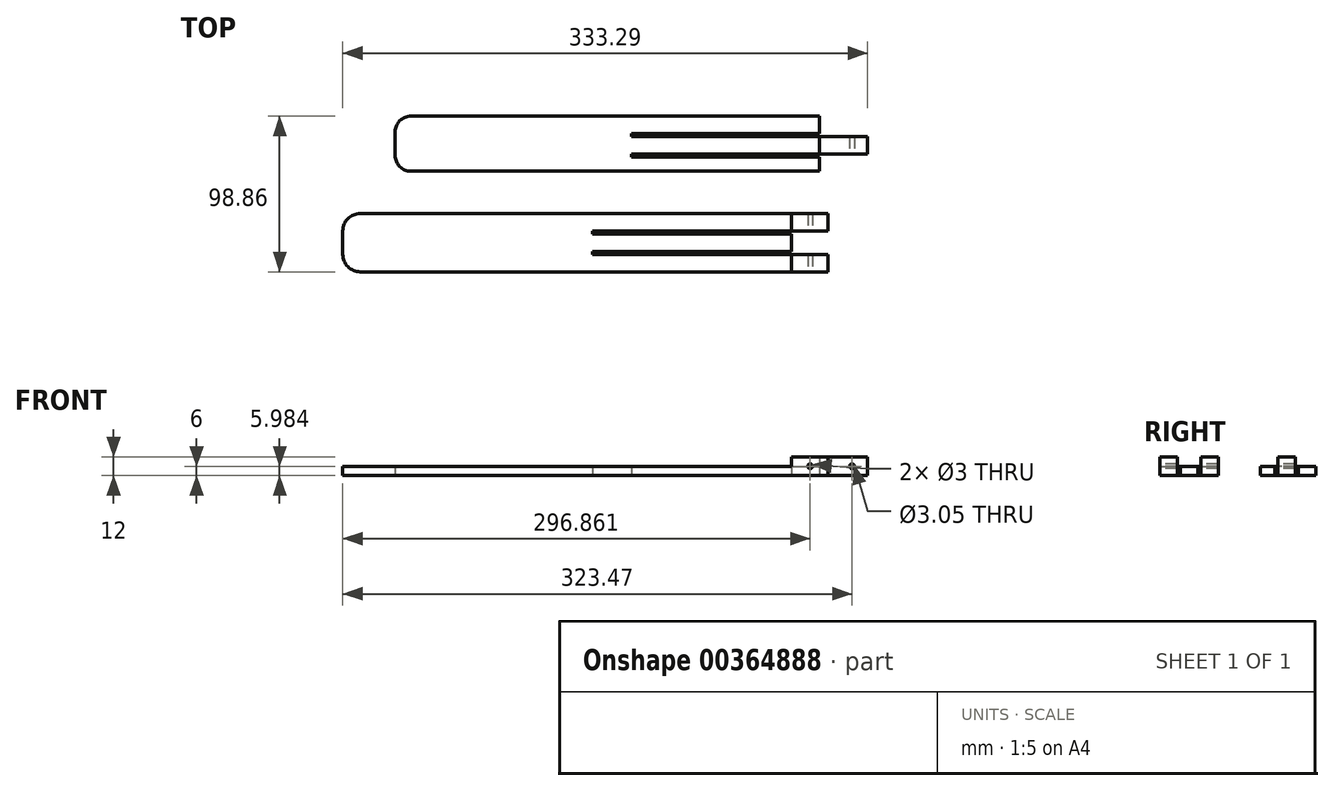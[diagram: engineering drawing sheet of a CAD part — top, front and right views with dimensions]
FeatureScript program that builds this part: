
annotation { "Feature Type Name" : "Feature", "Feature Type Description" : "" }
export const myFeature = defineFeature(function(context is Context, id is Id, definition is map)
    precondition{}
    {
        {
            var Q0;
            Q0=qCreatedBy(makeId("Top.planeOp"),FACE);
            var sketch = newSketch(context, id + "F0", { "sketchPlane" : qUnion([Q0])});
            skLineSegment(sketch, "E0.bottom", {"start": v(-150, 17.5) * mm, "end": v(119.34, 17.5) * mm});
            skLineSegment(sketch, "E0.top", {"start": v(-150, -17.5) * mm, "end": v(119.34, -17.5) * mm});
            skLineSegment(sketch, "E0.left", {"start": v(-150, 17.5) * mm, "end": v(-150, -17.5) * mm});
            skPoint(sketch, "E0.middle", {"position": v(0, 0) * mm});
            skLineSegment(sketch, "E1", {"start": v(0, 6.5) * mm, "end": v(119.34, 6.5) * mm});
            skLineSegment(sketch, "E2", {"start": v(0, 4.5) * mm, "end": v(150, 4.5) * mm});
            skLineSegment(sketch, "E3", {"start": v(0, -8.5) * mm, "end": v(119.34, -8.5) * mm});
            skLineSegment(sketch, "E4", {"start": v(0, -6.5) * mm, "end": v(150, -6.5) * mm});
            skLineSegment(sketch, "E5", {"start": v(0, -6.5) * mm, "end": v(0, -8.5) * mm});
            skLineSegment(sketch, "E6", {"start": v(0, 6.5) * mm, "end": v(0, 4.5) * mm});
            skLineSegment(sketch, "E7.trimOffspring", {"start": v(150, 4.5) * mm, "end": v(150, -6.5) * mm});
            skLineSegment(sketch, "E8", {"start": v(119.34, 17.5) * mm, "end": v(119.34, 6.5) * mm});
            skPoint(sketch, "E0.right.start.orphan", {"position": v(150, 17.5) * mm});
            skPoint(sketch, "E9.trimOffspring.start.orphan", {"position": v(150, -8.5) * mm});
            skPoint(sketch, "E10.orphan", {"position": v(150, -17.5) * mm});
            skLineSegment(sketch, "E11.trimOffspring", {"start": v(119.34, -8.5) * mm, "end": v(119.34, -17.5) * mm});
            skSolve(sketch);
        }
        {
            var Q0;
            Q0=makeQuery(id+"F0.imprint","IMPRINT",FACE,{"disambiguationData":[TD([[makeQuery(id+"F0.imprint","IMPRINT",EDGE,{"derivedFrom":sQuery(id+"F0.wireOp",EDGE,"E0.bottom")}),-1.0]])]});
            extrude(context, id + "F1", {"entities" : qUnion([Q0]), "depth" : 6 * mm});
        }
        {
            var Q0;
            Q0=makeQuery(id+"F1.opExtrude","SWEPT_EDGE",EDGE,{"disambiguationData":[OSD([sQuery(id+"F0.wireOp",EDGE,"E0.top"),sQuery(id+"F0.wireOp",EDGE,"E0.left")])]});
            var Q1;
            Q1=makeQuery(id+"F1.opExtrude","SWEPT_EDGE",EDGE,{"disambiguationData":[OSD([sQuery(id+"F0.wireOp",EDGE,"E0.bottom"),sQuery(id+"F0.wireOp",EDGE,"E0.left")])]});
            fillet(context, id + "F2", {"entities" : qUnion([Q0, Q1]), "radius" : 10 * mm, "tangentPropagation" : true, "allowEdgeOverflow" : false});
        }
        {
            var Q0;
            Q0=makeQuery(id+"F1.opExtrude","CAP_FACE",FACE,{"disambiguationData":[OSD([sQuery(id+"F0.wireOp",EDGE,"E0.bottom"),sQuery(id+"F0.wireOp",EDGE,"E0.top"),sQuery(id+"F0.wireOp",EDGE,"E0.left"),sQuery(id+"F0.wireOp",EDGE,"E1"),sQuery(id+"F0.wireOp",EDGE,"E2"),sQuery(id+"F0.wireOp",EDGE,"E3"),sQuery(id+"F0.wireOp",EDGE,"E4"),sQuery(id+"F0.wireOp",EDGE,"E5"),sQuery(id+"F0.wireOp",EDGE,"E6"),sQuery(id+"F0.wireOp",EDGE,"E7.trimOffspring"),sQuery(id+"F0.wireOp",EDGE,"E8"),sQuery(id+"F0.wireOp",EDGE,"E11.trimOffspring")])],"isStart":false});
            var sketch = newSketch(context, id + "F3", { "sketchPlane" : qUnion([Q0])});
            skLineSegment(sketch, "E12.bottom", {"start": v(119.34, 4.5) * mm, "end": v(150, 4.5) * mm});
            skLineSegment(sketch, "E12.top", {"start": v(119.34, -6.5) * mm, "end": v(150, -6.5) * mm});
            skLineSegment(sketch, "E12.left", {"start": v(119.34, 4.5) * mm, "end": v(119.34, -6.5) * mm});
            skLineSegment(sketch, "E12.right", {"start": v(150, 4.5) * mm, "end": v(150, -6.5) * mm});
            skSolve(sketch);
        }
        {
            var Q0;
            Q0=makeQuery(id+"F3.imprint","IMPRINT",FACE,{"disambiguationData":[TD([[makeQuery(id+"F3.imprint","IMPRINT",EDGE,{"derivedFrom":sQuery(id+"F3.wireOp",EDGE,"E12.bottom")}),-1.0]])]});
            extrude(context, id + "F4", {"entities" : qUnion([Q0]), "operationType" : NewBodyOperationType.ADD, "depth" : 6 * mm});
        }
        {
            var Q0;
            Q0=makeQuery(id+"F4.boolean.opBoolean","MERGE",FACE,{"derivedFrom":[makeQuery(id+"F1.opExtrude","SWEPT_FACE",FACE,{"disambiguationData":[OSD([sQuery(id+"F0.wireOp",EDGE,"E4")])]}),makeQuery(id+"F4.opExtrude","SWEPT_FACE",FACE,{"disambiguationData":[OSD([sQuery(id+"F3.wireOp",EDGE,"E12.top")])]})]});
            var sketch = newSketch(context, id + "F5", { "sketchPlane" : qUnion([Q0])});
            skCircle(sketch, "E13", {"center": v(140.18, 5.98) * mm, "radius": 1.53 * mm});
            skSolve(sketch);
        }
        {
            var Q0;
            Q0=makeQuery(id+"F5.imprint","IMPRINT",FACE,{"disambiguationData":[TD([[makeQuery(id+"F5.imprint","IMPRINT",EDGE,{"derivedFrom":sQuery(id+"F5.wireOp",EDGE,"E13")}),1.0]])]});
            extrude(context, id + "F6", {"entities" : qUnion([Q0]), "operationType" : NewBodyOperationType.REMOVE, "oppositeDirection" : true, "depth" : 11.4 * mm});
        }
        {
            var Q0;
            Q0=qCreatedBy(makeId("Top.planeOp"),FACE);
            var sketch = newSketch(context, id + "F7", { "sketchPlane" : qUnion([Q0])});
            skLineSegment(sketch, "E14.bottom", {"start": v(-183.29, -44.37) * mm, "end": v(124.88, -44.37) * mm});
            skLineSegment(sketch, "E14.top", {"start": v(-183.29, -81.36) * mm, "end": v(124.88, -81.36) * mm});
            skLineSegment(sketch, "E14.left", {"start": v(-183.29, -44.37) * mm, "end": v(-183.29, -81.36) * mm});
            skPoint(sketch, "E14.middle", {"position": v(-24.78, -62.86) * mm});
            skLineSegment(sketch, "E15", {"start": v(-24.78, -55.37) * mm, "end": v(124.88, -55.37) * mm});
            skLineSegment(sketch, "E16", {"start": v(-24.78, -57.37) * mm, "end": v(101.54, -57.37) * mm});
            skLineSegment(sketch, "E17", {"start": v(-24.78, -70.37) * mm, "end": v(124.88, -70.36) * mm});
            skLineSegment(sketch, "E18", {"start": v(-24.78, -68.37) * mm, "end": v(101.54, -68.37) * mm});
            skLineSegment(sketch, "E19", {"start": v(-24.78, -68.37) * mm, "end": v(-24.78, -70.37) * mm});
            skLineSegment(sketch, "E20", {"start": v(-24.78, -55.37) * mm, "end": v(-24.78, -57.37) * mm});
            skLineSegment(sketch, "E21.trimOffspring", {"start": v(101.54, -57.37) * mm, "end": v(101.54, -68.37) * mm});
            skLineSegment(sketch, "E22", {"start": v(124.88, -44.37) * mm, "end": v(124.88, -55.37) * mm});
            skPoint(sketch, "E14.right.start.orphan", {"position": v(133.73, -44.37) * mm});
            skPoint(sketch, "E23.trimOffspring.start.orphan", {"position": v(101.54, -70.36) * mm});
            skPoint(sketch, "E24.orphan", {"position": v(133.73, -81.36) * mm});
            skLineSegment(sketch, "E25.trimOffspring", {"start": v(124.88, -70.36) * mm, "end": v(124.88, -81.36) * mm});
            skSolve(sketch);
        }
        {
            var Q0;
            Q0=makeQuery(id+"F7.imprint","IMPRINT",FACE,{"disambiguationData":[TD([[makeQuery(id+"F7.imprint","IMPRINT",EDGE,{"derivedFrom":sQuery(id+"F7.wireOp",EDGE,"E14.bottom")}),-1.0]])]});
            extrude(context, id + "F8", {"entities" : qUnion([Q0]), "depth" : 6 * mm});
        }
        {
            var Q0;
            Q0=makeQuery(id+"F8.opExtrude","SWEPT_EDGE",EDGE,{"disambiguationData":[OSD([sQuery(id+"F7.wireOp",EDGE,"E14.top"),sQuery(id+"F7.wireOp",EDGE,"E14.left")])]});
            var Q1;
            Q1=makeQuery(id+"F8.opExtrude","SWEPT_EDGE",EDGE,{"disambiguationData":[OSD([sQuery(id+"F7.wireOp",EDGE,"E14.bottom"),sQuery(id+"F7.wireOp",EDGE,"E14.left")])]});
            fillet(context, id + "F9", {"entities" : qUnion([Q0, Q1]), "radius" : 11 * mm, "tangentPropagation" : true, "allowEdgeOverflow" : false});
        }
        {
            var Q0;
            Q0=makeQuery(id+"F8.opExtrude","CAP_FACE",FACE,{"disambiguationData":[OSD([sQuery(id+"F7.wireOp",EDGE,"E14.bottom"),sQuery(id+"F7.wireOp",EDGE,"E14.top"),sQuery(id+"F7.wireOp",EDGE,"E14.left"),sQuery(id+"F7.wireOp",EDGE,"E15"),sQuery(id+"F7.wireOp",EDGE,"E16"),sQuery(id+"F7.wireOp",EDGE,"E17"),sQuery(id+"F7.wireOp",EDGE,"E18"),sQuery(id+"F7.wireOp",EDGE,"E19"),sQuery(id+"F7.wireOp",EDGE,"E20"),sQuery(id+"F7.wireOp",EDGE,"E21.trimOffspring"),sQuery(id+"F7.wireOp",EDGE,"E22"),sQuery(id+"F7.wireOp",EDGE,"E25.trimOffspring")])],"isStart":false});
            var sketch = newSketch(context, id + "F10", { "sketchPlane" : qUnion([Q0])});
            skLineSegment(sketch, "E26.bottom", {"start": v(101.56, -55.37) * mm, "end": v(124.88, -55.37) * mm});
            skLineSegment(sketch, "E26.top", {"start": v(101.56, -44.37) * mm, "end": v(124.88, -44.37) * mm});
            skLineSegment(sketch, "E26.left", {"start": v(101.56, -55.37) * mm, "end": v(101.56, -44.37) * mm});
            skLineSegment(sketch, "E26.right", {"start": v(124.88, -55.37) * mm, "end": v(124.88, -44.37) * mm});
            skLineSegment(sketch, "E27.bottom", {"start": v(101.54, -81.36) * mm, "end": v(124.88, -81.36) * mm});
            skLineSegment(sketch, "E27.top", {"start": v(101.54, -70.36) * mm, "end": v(124.88, -70.36) * mm});
            skLineSegment(sketch, "E27.left", {"start": v(101.54, -81.36) * mm, "end": v(101.54, -70.36) * mm});
            skLineSegment(sketch, "E27.right", {"start": v(124.88, -81.36) * mm, "end": v(124.88, -70.36) * mm});
            skSolve(sketch);
        }
        {
            var Q0;
            Q0=makeQuery(id+"F10.imprint","IMPRINT",FACE,{"disambiguationData":[TD([[makeQuery(id+"F10.imprint","IMPRINT",EDGE,{"derivedFrom":sQuery(id+"F10.wireOp",EDGE,"E26.bottom")}),1.0]])]});
            var Q1;
            Q1=makeQuery(id+"F10.imprint","IMPRINT",FACE,{"disambiguationData":[TD([[makeQuery(id+"F10.imprint","IMPRINT",EDGE,{"derivedFrom":sQuery(id+"F10.wireOp",EDGE,"E27.bottom")}),1.0]])]});
            extrude(context, id + "F11", {"entities" : qUnion([Q0, Q1]), "operationType" : NewBodyOperationType.ADD, "depth" : 6 * mm});
        }
        {
            var Q0;
            Q0=makeQuery(id+"F11.boolean.opBoolean","MERGE",FACE,{"derivedFrom":[makeQuery(id+"F8.opExtrude","SWEPT_FACE",FACE,{"disambiguationData":[OSD([sQuery(id+"F7.wireOp",EDGE,"E14.top")])]}),makeQuery(id+"F11.opExtrude","SWEPT_FACE",FACE,{"disambiguationData":[OSD([sQuery(id+"F10.wireOp",EDGE,"E27.bottom")])]})]});
            var sketch = newSketch(context, id + "F12", { "sketchPlane" : qUnion([Q0])});
            skCircle(sketch, "E28", {"center": v(113.57, 6) * mm, "radius": 1.5 * mm});
            skPoint(sketch, "E28.centerSnap0", {"position": v(124.88, 6) * mm});
            skSolve(sketch);
        }
        {
            var Q0;
            Q0=makeQuery(id+"F12.imprint","IMPRINT",FACE,{"disambiguationData":[TD([[makeQuery(id+"F12.imprint","IMPRINT",EDGE,{"derivedFrom":sQuery(id+"F12.wireOp",EDGE,"E28")}),1.0]])]});
            extrude(context, id + "F13", {"entities" : qUnion([Q0]), "operationType" : NewBodyOperationType.REMOVE, "oppositeDirection" : true, "depth" : 46 * mm});
        }
    });
